# Revit family: Door_Service_FaceOfWallMount_Cookson
name_source: partatom
category: Doors
revit_build: Autodesk Revit MEP 2013 (Build: 20130531_2115(x64)
units: mm (PartAtom-declared; Revit-internal decimal feet)

## types (12) — shared parameters
04 CSI = 08 33 00
95 CSI = 08330
Assembly Code = B2030410
Coil Dimension Note = 14In to 22In -  Consult Cookson when dimensions are critical
Cost Note = Based on size, materials selected. Consult Cookson
Description = Built to order metal slatted rolling doors provide security against entry and/or weather protection
Distributor Locator = http://www.cooksondoor.com
Drip Extension = 0' - 3"
From Coil Side Operate on Left = No
From Coil Side Operate on Right = Yes
Function = Interior
Guide Height = 6' - 6 83/128"
Height = 8' - 0"
Jamb Dimension Note = 2 3/8In to  9 3/4In wide. Consult Cornell when dimensions are critical.
LEED Information = http://www.cooksondoor.com
Manufacturer = CornellCookson,Inc.
Model = ESD10
Mounting = Face of Wall
Operator Height = 5' - 4"
Optional Powder Coated Finish, standard RAL colors, Galv. Steel and Aluminum only = No
Optional aluminum, color anodized finish = No
Representative Disclaimer = Cookson products are sold and installed through a nationwide network of independent distributors
Revit Object Download Link = http://cornellcookson.smartbim.com
Sizing Disclaimer = 30’ wide, 30’ high standard construction. Larger Openings possible, consult factory
Subcategory = Roll Up
URL = http://www.cooksondoor.com
URL CAD = http://www.cooksondoor.com
URL Photographs = http://www.cooksondoor.com
URL Specifications = http://www.cooksondoor.com
Wall Closure = By host
Wall Construction = Masonry, Steel or Wood
Width = 6' - 0"
Windload = A full range of specific wind load requirements available- Consult Cookson.
zero-valued in all types: Cost

## per-type parameters (varying)
| type | Bottom Bar | Chain | Curtain 2 5/8" Slat | Guides | Hood | Motor | Operator |
| Hand-Chain Operated, Aluminium (Anodized Finish) | Aluminum, anodized finish (non-curtain components) | Yes | Aluminum, anodized finish (curtain only) | Aluminum, anodized finish (non-curtain components) | Aluminum, anodized finish (non-curtain components) | No | Operator : Hand-Chain |
| Hand-Chain Operated, Aluminium (Mill Finish) | Aluminum, mill finish (non-curtain components) | Yes | Aluminum, mill finish (curtain only) | Aluminum, mill finish (non-curtain components) | Aluminum, mill finish (non-curtain components) | No | Operator : Hand-Chain |
| Hand-Chain Operated, Galvanized Steel | Galvanized or powder coated plain steel (non curtain components) | Yes | Galvanized steel (curtain only) | Galvanized or powder coated plain steel (non curtain components) | Galvanized or powder coated plain steel (non curtain components) | No | Operator : Hand-Chain |
| Hand-Chain Operated, Stainless Steel | Stainless steel (non-curtain components) | Yes | Stainless steel (curtain only) | Stainless steel (non-curtain components) | Stainless steel (non-curtain components) | No | Operator : Hand-Chain |
| Motor Operated, Aluminium (Anodized Finish) | Aluminum, anodized finish (non-curtain components) | No | Aluminum, anodized finish (curtain only) | Aluminum, anodized finish (non-curtain components) | Aluminum, anodized finish (non-curtain components) | Yes | Operator : Motor Operator |
| Motor Operated, Aluminium (Mill Finish) | Aluminum, mill finish (non-curtain components) | No | Aluminum, mill finish (curtain only) | Aluminum, mill finish (non-curtain components) | Aluminum, mill finish (non-curtain components) | Yes | Operator : Motor Operator |
| Motor Operated, Galvanized Steel | Galvanized or powder coated plain steel (non curtain components) | No | Galvanized steel (curtain only) | Galvanized or powder coated plain steel (non curtain components) | Galvanized or powder coated plain steel (non curtain components) | Yes | Operator : Motor Operator |
| Motor Operated, Stainless Steel | Stainless steel (non-curtain components) | No | Stainless steel (curtain only) | Stainless steel (non-curtain components) | Stainless steel (non-curtain components) | Yes | Operator : Motor Operator |
| Push-Up Operated, Aluminium (Anodized Finish) | Aluminum, anodized finish (non-curtain components) | No | Aluminum, anodized finish (curtain only) | Aluminum, anodized finish (non-curtain components) | Aluminum, anodized finish (non-curtain components) | No | Operator : Push-UP |
| Push-Up Operated, Aluminium (Mill Finish) | Aluminum, mill finish (non-curtain components) | No | Aluminum, mill finish (curtain only) | Aluminum, mill finish (non-curtain components) | Aluminum, mill finish (non-curtain components) | No | Operator : Push-UP |
| Push-Up Operated, Galvanized Steel | Galvanized or powder coated plain steel (non curtain components) | No | Galvanized steel (curtain only) | Galvanized or powder coated plain steel (non curtain components) | Galvanized or powder coated plain steel (non curtain components) | No | Operator : Push-UP |
| Push-Up Operated, Stainless Steel | Stainless steel (non-curtain components) | No | Stainless steel (curtain only) | Stainless steel (non-curtain components) | Stainless steel (non-curtain components) | No | Operator : Push-UP |

## geometry (parser evidence)
native form markers: Blend x52, Sweep x10
no freeform markers — native parametric forms only
